# Revit family: VS F Atlantis
name_source: partatom
category: Plumbing Fixtures
revit_build: Autodesk Revit 2015 (Build: 20140322_1515(x64)
units: mm (PartAtom-declared; Revit-internal decimal feet)

## types (1)
- VS F Atlantis
    Assembly Code = D2010.60
    BT_Color = Blanco
    BT_Itemizado_Estandar_CDT = E 04 02 80
    BT_Material = Loza
    BT_SKU = 00 00 00
    BT_Uso = Baño
    Depth = 515 mm
    Description = Vaso para fluxor empotrado
Modelo: ATLANTIS
Instalación: A piso BTW
Descarga:
Muro: 180 mm
Altura: 380 mm (sin asiento)
Fijación piso: Incluida
Asiento con tapa incluido
    Height = 380 mm
    ID_Objeto = BT_F_F_1791
    ID_Source = BIMTOOL
    Keynote = 22 41 13.13
    Manufacturer = Klipen
    Model = VS F Atlantis
    Supplier = Mk
    Type Comments = Vaso para fluxor empotrado
Modelo: ATLANTIS
Instalación: A piso BTW
    URL = www.mk.cl
    Width = 515 mm

## geometry (parser evidence)
native form markers: Blend x6, Extrusion x2, Sweep x4
no freeform markers — native parametric forms only
